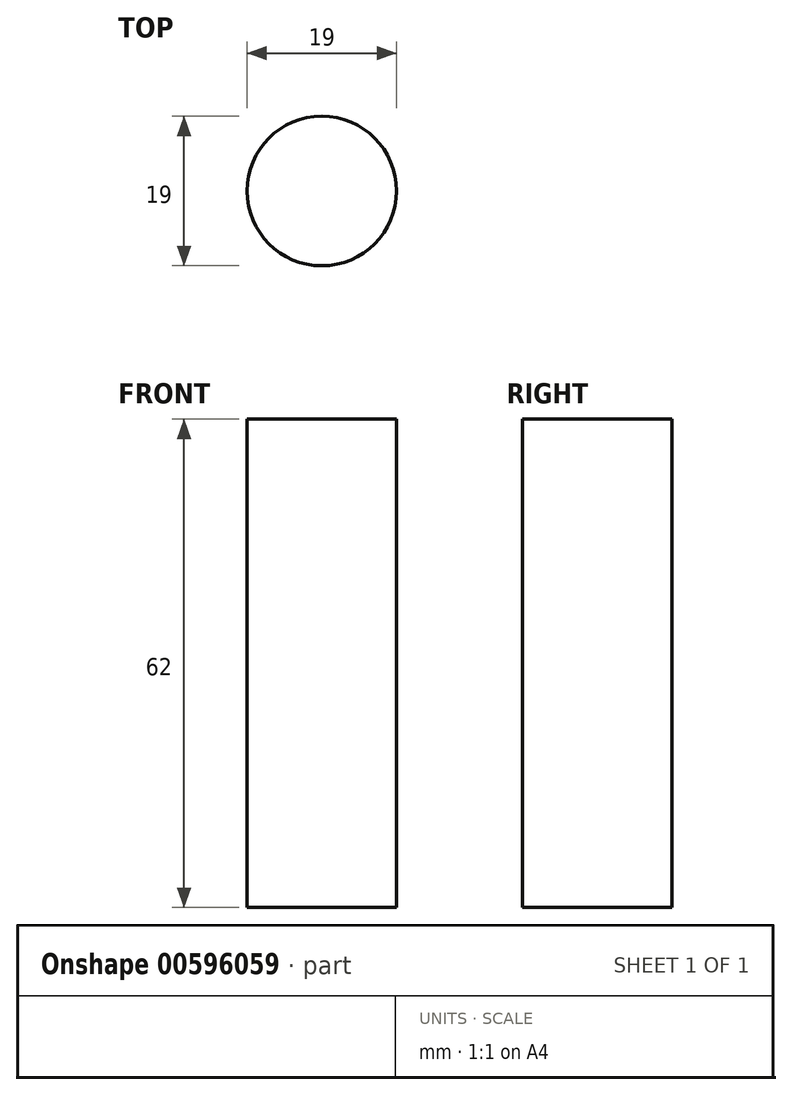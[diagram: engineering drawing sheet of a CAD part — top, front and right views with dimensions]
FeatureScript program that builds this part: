
annotation { "Feature Type Name" : "Feature", "Feature Type Description" : "" }
export const myFeature = defineFeature(function(context is Context, id is Id, definition is map)
    precondition{}
    {
        {
            var Q0;
            Q0=qCreatedBy(makeId("Right.planeOp"),FACE);
            var sketch = newSketch(context, id + "F0", { "sketchPlane" : qUnion([Q0])});
            skLineSegment(sketch, "E0.bottom", {"start": v(0, 0) * mm, "end": v(17.33, 0) * mm});
            skLineSegment(sketch, "E0.left", {"start": v(0, 0) * mm, "end": v(0, 38.4) * mm});
            skLineSegment(sketch, "E0.right", {"start": v(17.33, 0) * mm, "end": v(17.33, 46.1) * mm});
            skLineSegment(sketch, "E1", {"start": v(0, 38.4) * mm, "end": v(0, 83.4) * mm});
            skArc(sketch, "E2", {"start": v(17.33, 46.1) * mm, "mid": v(12.79, 66.66) * mm, "end": v(0, 83.4) * mm});
            skLineSegment(sketch, "E3.bottom", {"start": v(0, 0) * mm, "end": v(9.5, 0) * mm});
            skLineSegment(sketch, "E3.top", {"start": v(0, 62) * mm, "end": v(9.5, 62) * mm});
            skLineSegment(sketch, "E3.left", {"start": v(0, 0) * mm, "end": v(0, 62) * mm});
            skLineSegment(sketch, "E3.right", {"start": v(9.5, 0) * mm, "end": v(9.5, 62) * mm});
            skSolve(sketch);
        }
        {
            var Q0;
            Q0=makeQuery(id+"F0.imprint","IMPRINT",FACE,{"disambiguationData":[TD([[makeQuery(id+"F0.imprint","IMPRINT",EDGE,{"derivedFrom":sQuery(id+"F0.wireOp",EDGE,"E0.bottom")}),1.0]])]});
            var Q1;
            Q1=sQuery(id+"F0.wireOp",EDGE,"E1");
            revolve(context, id + "F1", {"entities" : qUnion([Q0]), "axis" : qUnion([Q1]), "revolveType" : RevolveType.FULL});
        }
    });
